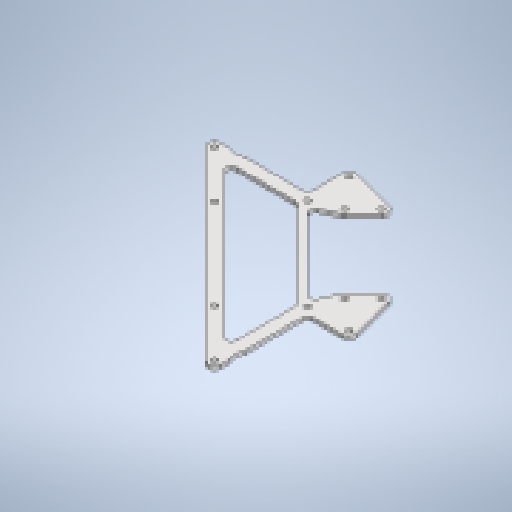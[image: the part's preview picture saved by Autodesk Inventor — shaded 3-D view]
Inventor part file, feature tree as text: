
AUTODESK INVENTOR PART (.ipt)
format: ipt  version: 2025.1 (Build 291241000, 241)  size: 312,320 bytes
history: native  units: mm
features: other x7, extrude x7, sketch x7, reference x4, fillet x3, projected_geometry x2
ambient origin geometry x8: Origin, YZ Plane, XZ Plane, XY Plane, X Axis, Y Axis, Z Axis, Center Point
bodies: Body1 (feature_tree)
feature tree (30):
  other  "ソリッド1"
  extrude  "押し出し1"  Depth=36.0mm
  fillet  "フィレット1"  Radius=2.2mm
  extrude  "押し出し2"  Depth=2.2mm
  other  "作業平面1"
  extrude  "押し出し3"  Depth=5.0mm
  extrude  "押し出し5"  Depth=1.5mm TaperAngle=0.0deg
  fillet  "フィレット2"  Radius=2.0mm
  extrude  "押し出し6"  Depth=16.0mm
  extrude  "押し出し7"  TaperAngle=45.0deg  [1 undecoded]
  fillet  "フィレット3"  Radius=3.0mm
  extrude  "押し出し8"  Depth=2.2mm
  sketch  "スケッチ1"
  sketch  "スケッチ2"
  projected_geometry  "投影ループ1"
  sketch  "スケッチ3"
  reference  "参照1"
  reference  "参照2"
  projected_geometry  "投影ループ2"
  sketch  "スケッチ4"
  sketch  "スケッチ5"
  reference  "参照3"
  reference  "参照4"
  sketch  "スケッチ6"
  sketch  "スケッチ7"
  other  "<userpath>\Documents\Inventor\Vixen\kosi_v2.iam"
  other  "kosi_v2.iam"
  other  "senakamata:1"
  other  "KRS2500_scale:1"
  other  "KRS2500_scale:2"
note: 1 required parameter value undecoded (feature->parameter linkage not recoverable at this tier; creation-order binding heuristic only, values carry confidence <= 0.55)
